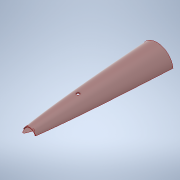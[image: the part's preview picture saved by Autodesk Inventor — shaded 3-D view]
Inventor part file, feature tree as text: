
AUTODESK INVENTOR PART (.ipt)
format: ipt  version: 2020.3 (Build 243373000, 373)  size: 342,528 bytes
history: native  units: mm
features: extrude x3, fillet x3, sketch x2, revolve x2
ambient origin geometry x8: Origin, YZ Plane, XZ Plane, XY Plane, X Axis, Y Axis, Z Axis, Center Point
bodies: Body1 (feature_tree)
feature tree (10):
  sketch  "Sketch3"  dims[d54=25.9mm d55=5.0mm d56=0.9mm d57=2.0mm d58=25.9mm d59=5.0mm d60=0.9mm d61=212.5mm d62=250.0mm d63=25.0mm d64=25.0mm d65=248.2mm d66=25.0mm d67=2.0mm d68=212.5mm d69=5.0mm d70=8.0mm d71=212.5mm d72=15.232132mm d73=360.0deg]
  revolve  "Revolution5"  Angle=360.0deg
  extrude  "Extrusion5"  Depth=3.0mm
  extrude  "Extrusion7"  Depth=2.0mm
  revolve  "Revolution6"  [1 undecoded]
  extrude  "Extrusion8"  Depth=3.0mm
  fillet  "Fillet1"  Radius=256.25mm
  fillet  "Fillet2"  [1 undecoded]
  fillet  "Fillet3"  Radius=5.0mm
  sketch  "Sketch5"  dims[d74=60.0mm d75=0.0mm d78=3.0mm d79=2.0mm d80=14.0mm d81=0.0mm d82=3.0mm d83=256.25mm d84=360.0deg d85=5.0mm d86=25.0mm d87=0.0mm d88=2.0mm d89=2.0mm d90=2.0mm d7=0.872665mm d8=0.872665mm d21=0.5mm d22=0.872665mm d23=0.5mm d24=0.872665mm]
note: 2 required parameter values undecoded (feature->parameter linkage not recoverable at this tier; creation-order binding heuristic only, values carry confidence <= 0.55)